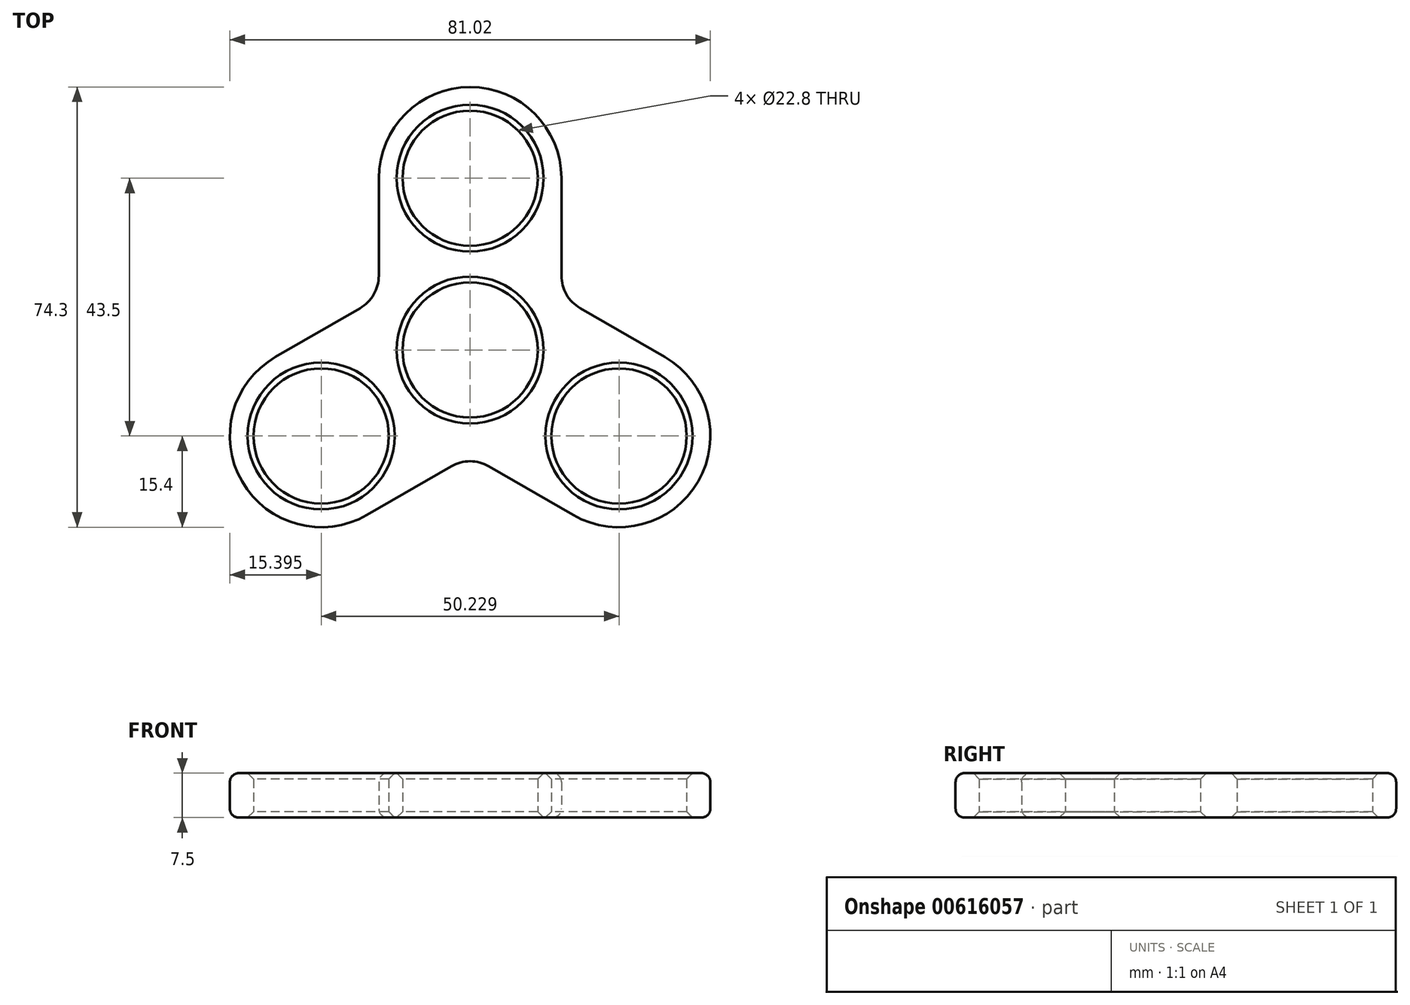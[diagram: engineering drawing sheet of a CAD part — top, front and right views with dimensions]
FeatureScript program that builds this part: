
annotation { "Feature Type Name" : "Feature", "Feature Type Description" : "" }
export const myFeature = defineFeature(function(context is Context, id is Id, definition is map)
    precondition{}
    {
        {
            var Q0;
            Q0=qCreatedBy(makeId("Top.planeOp"),FACE);
            var sketch = newSketch(context, id + "F0", { "sketchPlane" : qUnion([Q0])});
            skCircle(sketch, "E0", {"center": v(0, 0) * mm, "radius": 11.4 * mm});
            skCircle(sketch, "E1", {"center": v(0, 29) * mm, "radius": 11.4 * mm});
            skArc(sketch, "E2.0", {"start": v(15.4, 29) * mm, "mid": v(0, 44.4) * mm, "end": v(-15.4, 29) * mm});
            skCircle(sketch, "E3.0", {"center": v(0, 0) * mm, "radius": 15.4 * mm, "construction": true});
            skLineSegment(sketch, "E4", {"start": v(-15.4, 29) * mm, "end": v(-15.4, 12.56) * mm});
            skLineSegment(sketch, "E5", {"start": v(15.4, 29) * mm, "end": v(15.4, 12.56) * mm});
            skCircle(sketch, "E6.1.1", {"center": v(-25.11, -14.5) * mm, "radius": 11.4 * mm});
            skLineSegment(sketch, "E6.1.2", {"start": v(-17.41, -27.84) * mm, "end": v(-3.18, -19.62) * mm});
            skLineSegment(sketch, "E6.1.3", {"start": v(-32.81, -1.16) * mm, "end": v(-18.58, 7.06) * mm});
            skArc(sketch, "E6.2.0", {"start": v(17.41, -27.84) * mm, "mid": v(38.45, -22.2) * mm, "end": v(32.81, -1.16) * mm});
            skCircle(sketch, "E6.2.1", {"center": v(25.11, -14.5) * mm, "radius": 11.4 * mm});
            skLineSegment(sketch, "E6.2.2", {"start": v(32.81, -1.16) * mm, "end": v(18.57, 7.06) * mm});
            skLineSegment(sketch, "E6.2.3", {"start": v(17.41, -27.84) * mm, "end": v(3.17, -19.62) * mm});
            skPoint(sketch, "E7.newPointA", {"position": v(-7.7, 13.34) * mm});
            skPoint(sketch, "E7.newPointB", {"position": v(-15.4, 0) * mm});
            skArc(sketch, "E7.filletArc", {"start": v(-18.58, 7.06) * mm, "mid": v(-16.25, 9.38) * mm, "end": v(-15.4, 12.56) * mm});
            skPoint(sketch, "E8.newPointA", {"position": v(15.4, 0) * mm});
            skPoint(sketch, "E8.newPointB", {"position": v(7.7, 13.34) * mm});
            skArc(sketch, "E8.filletArc", {"start": v(15.4, 12.56) * mm, "mid": v(16.25, 9.38) * mm, "end": v(18.57, 7.06) * mm});
            skPoint(sketch, "E9.newPointA", {"position": v(-7.7, -13.34) * mm});
            skPoint(sketch, "E9.newPointB", {"position": v(7.7, -13.34) * mm});
            skArc(sketch, "E9.filletArc", {"start": v(3.17, -19.62) * mm, "mid": v(0, -18.76) * mm, "end": v(-3.18, -19.62) * mm});
            skArc(sketch, "E10", {"start": v(-32.81, -1.16) * mm, "mid": v(-38.45, -22.2) * mm, "end": v(-17.41, -27.84) * mm});
            skSolve(sketch);
        }
        {
            var Q0;
            Q0=makeQuery(id+"F0.imprint","IMPRINT",FACE,{"disambiguationData":[TD([[makeQuery(id+"F0.imprint","IMPRINT",EDGE,{"derivedFrom":sQuery(id+"F0.wireOp",EDGE,"E0")}),-1.0]])]});
            extrude(context, id + "F1", {"entities" : qUnion([Q0]), "depth" : 7.5 * mm, "offsetDistance" : 25 * mm});
        }
        {
            var Q0;
            Q0=makeQuery(id+"F1.opExtrude","CAP_EDGE",EDGE,{"disambiguationData":[OSD([sQuery(id+"F0.wireOp",EDGE,"E7.filletArc")])],"isStart":true});
            var Q1;
            Q1=makeQuery(id+"F1.opExtrude","SWEPT_EDGE",EDGE,{"disambiguationData":[OSD([sQuery(id+"F0.wireOp",EDGE,"E5"),sQuery(id+"F0.wireOp",EDGE,"E8.filletArc")])]});
            var Q2;
            Q2=makeQuery(id+"F1.opExtrude","CAP_EDGE",EDGE,{"disambiguationData":[OSD([sQuery(id+"F0.wireOp",EDGE,"E6.2.2")])],"isStart":false});
            fillet(context, id + "F2", {"entities" : qUnion([Q0, Q1, Q2]), "radius" : 1.5 * mm, "tangentPropagation" : true, "allowEdgeOverflow" : false});
        }
        {
            var Q0;
            Q0=makeQuery(id+"F1.opExtrude","CAP_EDGE",EDGE,{"disambiguationData":[OSD([sQuery(id+"F0.wireOp",EDGE,"E1")])],"isStart":false});
            var Q1;
            Q1=makeQuery(id+"F1.opExtrude","CAP_EDGE",EDGE,{"disambiguationData":[OSD([sQuery(id+"F0.wireOp",EDGE,"E0")])],"isStart":true});
            var Q2;
            Q2=makeQuery(id+"F1.opExtrude","CAP_EDGE",EDGE,{"disambiguationData":[OSD([sQuery(id+"F0.wireOp",EDGE,"E0")])],"isStart":false});
            var Q3;
            Q3=makeQuery(id+"F1.opExtrude","CAP_EDGE",EDGE,{"disambiguationData":[OSD([sQuery(id+"F0.wireOp",EDGE,"E6.2.1")])],"isStart":true});
            var Q4;
            Q4=makeQuery(id+"F1.opExtrude","CAP_EDGE",EDGE,{"disambiguationData":[OSD([sQuery(id+"F0.wireOp",EDGE,"E6.2.1")])],"isStart":false});
            var Q5;
            Q5=makeQuery(id+"F1.opExtrude","CAP_EDGE",EDGE,{"disambiguationData":[OSD([sQuery(id+"F0.wireOp",EDGE,"E6.1.1")])],"isStart":false});
            var Q6;
            Q6=makeQuery(id+"F1.opExtrude","CAP_EDGE",EDGE,{"disambiguationData":[OSD([sQuery(id+"F0.wireOp",EDGE,"E6.1.1")])],"isStart":true});
            var Q7;
            Q7=makeQuery(id+"F1.opExtrude","CAP_EDGE",EDGE,{"disambiguationData":[OSD([sQuery(id+"F0.wireOp",EDGE,"E1")])],"isStart":true});
            chamfer(context, id + "F3", {"entities" : qUnion([Q0, Q1, Q2, Q3, Q4, Q5, Q6, Q7]), "width" : 1 * mm, "tangentPropagation" : true});
        }
    });
